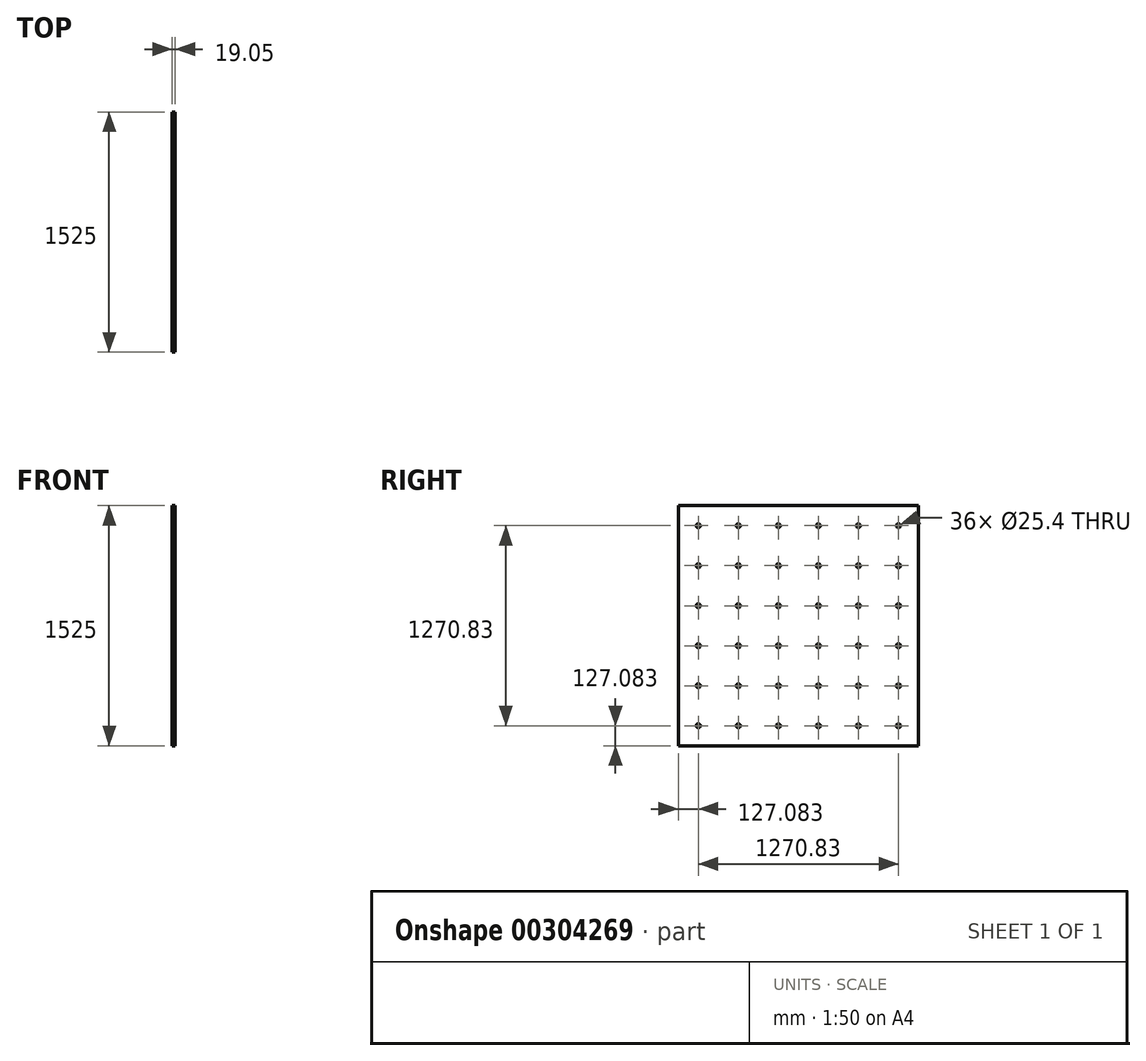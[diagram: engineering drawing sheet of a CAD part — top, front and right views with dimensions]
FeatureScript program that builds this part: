
annotation { "Feature Type Name" : "Feature", "Feature Type Description" : "" }
export const myFeature = defineFeature(function(context is Context, id is Id, definition is map)
    precondition{}
    {
        {
            var Q0;
            Q0=qCreatedBy(makeId("Right.planeOp"),FACE);
            var sketch = newSketch(context, id + "F0", { "sketchPlane" : qUnion([Q0])});
            skLineSegment(sketch, "E0.bottom", {"start": v(0, 0) * mm, "end": v(1525, 0) * mm});
            skLineSegment(sketch, "E0.top", {"start": v(0, 1525) * mm, "end": v(1525, 1525) * mm});
            skLineSegment(sketch, "E0.left", {"start": v(0, 0) * mm, "end": v(0, 1525) * mm});
            skLineSegment(sketch, "E0.right", {"start": v(1525, 0) * mm, "end": v(1525, 1525) * mm});
            skPoint(sketch, "E0.middle", {"position": v(762.5, 762.5) * mm});
            skSolve(sketch);
        }
        {
            var Q0;
            Q0=qSketchRegion(id+"F0",true);
            extrude(context, id + "F1", {"entities" : qUnion([Q0]), "depth" : 19.05 * mm});
        }
        {
            var Q0;
            Q0=makeQuery(id+"F1.opExtrude","CAP_FACE",FACE,{"disambiguationData":[OSD([sQuery(id+"F0.wireOp",EDGE,"E0.bottom"),sQuery(id+"F0.wireOp",EDGE,"E0.top"),sQuery(id+"F0.wireOp",EDGE,"E0.left"),sQuery(id+"F0.wireOp",EDGE,"E0.right")])],"isStart":true});
            var sketch = newSketch(context, id + "F2", { "sketchPlane" : qUnion([Q0])});
            skCircle(sketch, "E1", {"center": v(-1397.92, 1397.92) * mm, "radius": 12.7 * mm});
            skCircle(sketch, "E2.0.1.0", {"center": v(-1397.92, 1143.75) * mm, "radius": 12.7 * mm});
            skCircle(sketch, "E2.0.2.0", {"center": v(-1397.92, 889.58) * mm, "radius": 12.7 * mm});
            skCircle(sketch, "E2.0.3.0", {"center": v(-1397.92, 635.42) * mm, "radius": 12.7 * mm});
            skCircle(sketch, "E2.0.4.0", {"center": v(-1397.92, 381.25) * mm, "radius": 12.7 * mm});
            skCircle(sketch, "E2.0.5.0", {"center": v(-1397.92, 127.08) * mm, "radius": 12.7 * mm});
            skCircle(sketch, "E2.1.0.0", {"center": v(-1143.75, 1397.92) * mm, "radius": 12.7 * mm});
            skCircle(sketch, "E2.1.1.0", {"center": v(-1143.75, 1143.75) * mm, "radius": 12.7 * mm});
            skCircle(sketch, "E2.1.2.0", {"center": v(-1143.75, 889.58) * mm, "radius": 12.7 * mm});
            skCircle(sketch, "E2.1.3.0", {"center": v(-1143.75, 635.42) * mm, "radius": 12.7 * mm});
            skCircle(sketch, "E2.1.4.0", {"center": v(-1143.75, 381.25) * mm, "radius": 12.7 * mm});
            skCircle(sketch, "E2.1.5.0", {"center": v(-1143.75, 127.08) * mm, "radius": 12.7 * mm});
            skCircle(sketch, "E2.2.0.0", {"center": v(-889.58, 1397.92) * mm, "radius": 12.7 * mm});
            skCircle(sketch, "E2.2.1.0", {"center": v(-889.58, 1143.75) * mm, "radius": 12.7 * mm});
            skCircle(sketch, "E2.2.2.0", {"center": v(-889.58, 889.58) * mm, "radius": 12.7 * mm});
            skCircle(sketch, "E2.2.3.0", {"center": v(-889.58, 635.42) * mm, "radius": 12.7 * mm});
            skCircle(sketch, "E2.2.4.0", {"center": v(-889.58, 381.25) * mm, "radius": 12.7 * mm});
            skCircle(sketch, "E2.2.5.0", {"center": v(-889.58, 127.08) * mm, "radius": 12.7 * mm});
            skLineSegment(sketch, "E2.direction1", {"start": v(-1397.92, 1397.92) * mm, "end": v(-1143.75, 1397.92) * mm, "construction": true});
            skLineSegment(sketch, "E2.direction2", {"start": v(-1397.92, 1397.92) * mm, "end": v(-1397.92, 1143.75) * mm, "construction": true});
            skLineSegment(sketch, "E3", {"start": v(-1397.92, 1397.92) * mm, "end": v(-1525, 1397.92) * mm, "construction": true});
            skLineSegment(sketch, "E4", {"start": v(-1397.92, 1397.92) * mm, "end": v(-1397.92, 1525) * mm, "construction": true});
            skLineSegment(sketch, "E5", {"start": v(-1270.83, 1397.92) * mm, "end": v(-1270.83, 1270.83) * mm, "construction": true});
            skLineSegment(sketch, "E6", {"start": v(-1270.83, 1270.83) * mm, "end": v(-1397.92, 1270.83) * mm, "construction": true});
            skCircle(sketch, "E7.0.3.0", {"center": v(-635.42, 1397.92) * mm, "radius": 12.7 * mm});
            skCircle(sketch, "E7.0.3.1", {"center": v(-635.42, 1143.75) * mm, "radius": 12.7 * mm});
            skCircle(sketch, "E7.0.3.2", {"center": v(-635.42, 889.58) * mm, "radius": 12.7 * mm});
            skCircle(sketch, "E7.0.3.3", {"center": v(-635.42, 635.42) * mm, "radius": 12.7 * mm});
            skCircle(sketch, "E7.0.3.4", {"center": v(-635.42, 381.25) * mm, "radius": 12.7 * mm});
            skCircle(sketch, "E7.0.3.5", {"center": v(-635.42, 127.08) * mm, "radius": 12.7 * mm});
            skCircle(sketch, "E8.0.4.0", {"center": v(-381.25, 1397.92) * mm, "radius": 12.7 * mm});
            skCircle(sketch, "E8.0.4.1", {"center": v(-381.25, 1143.75) * mm, "radius": 12.7 * mm});
            skCircle(sketch, "E8.0.4.2", {"center": v(-381.25, 889.58) * mm, "radius": 12.7 * mm});
            skCircle(sketch, "E8.0.4.3", {"center": v(-381.25, 635.42) * mm, "radius": 12.7 * mm});
            skCircle(sketch, "E8.0.4.4", {"center": v(-381.25, 381.25) * mm, "radius": 12.7 * mm});
            skCircle(sketch, "E8.0.4.5", {"center": v(-381.25, 127.08) * mm, "radius": 12.7 * mm});
            skCircle(sketch, "E9.0.5.0", {"center": v(-127.08, 1397.92) * mm, "radius": 12.7 * mm});
            skCircle(sketch, "E9.0.5.1", {"center": v(-127.08, 1143.75) * mm, "radius": 12.7 * mm});
            skCircle(sketch, "E9.0.5.2", {"center": v(-127.08, 889.58) * mm, "radius": 12.7 * mm});
            skCircle(sketch, "E9.0.5.3", {"center": v(-127.08, 635.42) * mm, "radius": 12.7 * mm});
            skCircle(sketch, "E9.0.5.4", {"center": v(-127.08, 381.25) * mm, "radius": 12.7 * mm});
            skCircle(sketch, "E9.0.5.5", {"center": v(-127.08, 127.08) * mm, "radius": 12.7 * mm});
            skLineSegment(sketch, "E10", {"start": v(-127.08, 127.08) * mm, "end": v(-127.08, 0) * mm, "construction": true});
            skLineSegment(sketch, "E11", {"start": v(-127.08, 127.08) * mm, "end": v(0, 127.08) * mm, "construction": true});
            skSolve(sketch);
        }
        {
            var Q0;
            Q0=qSketchRegion(id+"F2",true);
            extrude(context, id + "F3", {"entities" : qUnion([Q0]), "operationType" : NewBodyOperationType.REMOVE, "depth" : 381 * mm, "hasSecondDirection" : true, "secondDirectionOppositeDirection" : true, "secondDirectionDepth" : 25.4 * mm});
        }
    });
